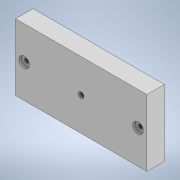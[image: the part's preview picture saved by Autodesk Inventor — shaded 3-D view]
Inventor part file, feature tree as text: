
AUTODESK INVENTOR PART (.ipt)
format: ipt  version: 2022.2 (Build 262287030, 287C)  size: 112,640 bytes
history: native  units: in
note: dims shown in document units (in); Inventor stores cm internally (conversion verified against a paired STEP export)
features: sketch x3, hole x2, extrude x1, projected_geometry x1
ambient origin geometry x8: Origin, YZ Plane, XZ Plane, XY Plane, X Axis, Y Axis, Z Axis, Center Point
bodies: Solid1 (feature_tree)
feature tree (7):
  extrude  "Extrusion1"  Depth=1.4961in
  hole  "Hole2"  [1 undecoded]
  hole  "Hole3"  [1 undecoded]
  sketch  "Sketch1"  dims[d0=0.3937in d1=0.0in d2=1.4961in]
  sketch  "Sketch3"  dims[d3=2.9528in]
  sketch  "Sketch4"  dims[d69=0.125in d70=0.2953in d71=0.1476in d72=0.0984in d73=90.0deg d74=0.1969in d75=0.8108in d76=0.1969in d77=0.7874in d79=2.5591in d80=0.3937in d82=0.3937in d84=0.0968in d85=0.2362in d86=0.2362in d87=0.0551in d88=90.0deg d89=0.1969in d90=0.8108in d62=0.3937in d63=0.3937in d64=0.3937in d65=0.0591in d66=0.0984in d67=0.1476in d68=0.5635in]
  projected_geometry  "Projected Loop2"
note: 2 required parameter values undecoded (feature->parameter linkage not recoverable at this tier; creation-order binding heuristic only, values carry confidence <= 0.55)
